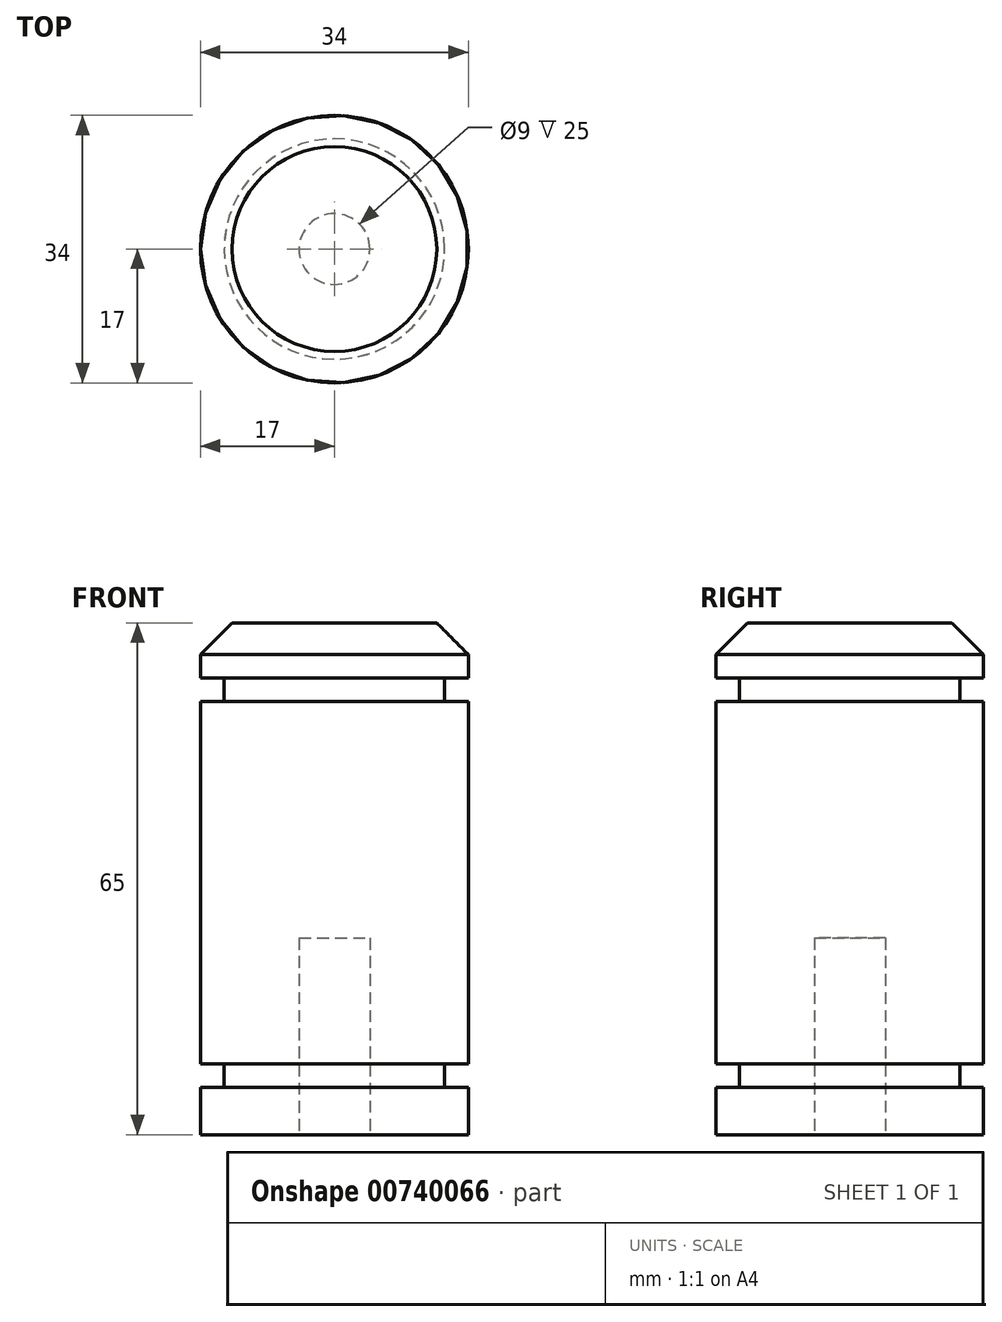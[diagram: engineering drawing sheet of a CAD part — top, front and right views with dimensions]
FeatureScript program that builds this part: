
annotation { "Feature Type Name" : "Feature", "Feature Type Description" : "" }
export const myFeature = defineFeature(function(context is Context, id is Id, definition is map)
    precondition{}
    {
        {
            var Q0;
            Q0=qCreatedBy(makeId("Top.planeOp"),FACE);
            var sketch = newSketch(context, id + "F0", { "sketchPlane" : qUnion([Q0])});
            skCircle(sketch, "E0", {"center": v(0, 0) * mm, "radius": 17 * mm});
            skSolve(sketch);
        }
        {
            var Q0;
            Q0 = qSketchRegion(id + "F0", true);
            extrude(context, id + "F1", {"entities" : qUnion([Q0]), "depth" : 65 * mm, "offsetDistance" : 25 * mm});
        }
        {
            var Q0;
            Q0=makeQuery(id+"F1.opExtrude","CAP_EDGE",EDGE,{"disambiguationData":[OSD([sQuery(id+"F0.wireOp",EDGE,"E0")])],"isStart":false});
            chamfer(context, id + "F2", {"entities" : qUnion([Q0]), "width" : 4 * mm, "tangentPropagation" : true});
        }
        {
            var Q0;
            Q0=makeQuery(id+"F1.opExtrude","CAP_FACE",FACE,{"disambiguationData":[OSD([sQuery(id+"F0.wireOp",EDGE,"E0")])],"isStart":true});
            var sketch = newSketch(context, id + "F3", { "sketchPlane" : qUnion([Q0])});
            skCircle(sketch, "E1", {"center": v(0, 0) * mm, "radius": 4.5 * mm});
            skSolve(sketch);
        }
        {
            var Q0;
            Q0=makeQuery(id+"F3.imprint","IMPRINT",FACE,{"disambiguationData":[TD([[makeQuery(id+"F3.imprint","IMPRINT",EDGE,{"derivedFrom":sQuery(id+"F3.wireOp",EDGE,"E1")}),1.0]])]});
            extrude(context, id + "F4", {"entities" : qUnion([Q0]), "operationType" : NewBodyOperationType.REMOVE, "oppositeDirection" : true, "depth" : 25 * mm, "offsetDistance" : 25 * mm});
        }
        {
            var Q0;
            Q0=qCreatedBy(makeId("Front.planeOp"),FACE);
            var sketch = newSketch(context, id + "F5", { "sketchPlane" : qUnion([Q0])});
            skLineSegment(sketch, "E2.bottom", {"start": v(17, 9) * mm, "end": v(14, 9) * mm});
            skLineSegment(sketch, "E2.top", {"start": v(17, 6) * mm, "end": v(14, 6) * mm});
            skLineSegment(sketch, "E2.left", {"start": v(17, 9) * mm, "end": v(17, 6) * mm});
            skLineSegment(sketch, "E2.right", {"start": v(14, 9) * mm, "end": v(14, 6) * mm});
            skSolve(sketch);
        }
        {
            var Q0;
            Q0 = qSketchRegion(id + "F5", true);
            var Q1;
            Q1=makeQuery(id+"F1.opExtrude","SWEPT_FACE",FACE,{"disambiguationData":[OSD([sQuery(id+"F0.wireOp",EDGE,"E0")])]});
            revolve(context, id + "F6", {"operationType" : NewBodyOperationType.REMOVE, "surfaceOperationType" : NewSurfaceOperationType.NEW, "entities" : qUnion([Q0]), "axis" : qUnion([Q1]), "revolveType" : RevolveType.FULL, "oppositeDirection" : true});
        }
        {
            var Q0;
            Q0=qCreatedBy(makeId("Right.planeOp"),FACE);
            var sketch = newSketch(context, id + "F7", { "sketchPlane" : qUnion([Q0])});
            skLineSegment(sketch, "E3.bottom", {"start": v(-17, 58) * mm, "end": v(-14, 58) * mm});
            skLineSegment(sketch, "E3.top", {"start": v(-17, 55) * mm, "end": v(-14, 55) * mm});
            skLineSegment(sketch, "E3.left", {"start": v(-17, 58) * mm, "end": v(-17, 55) * mm});
            skLineSegment(sketch, "E3.right", {"start": v(-14, 58) * mm, "end": v(-14, 55) * mm});
            skSolve(sketch);
        }
        {
            var Q0;
            Q0 = qSketchRegion(id + "F7", true);
            var Q1;
            {var subQ0=sQuery(id+"F0.wireOp",EDGE,"E0");Q1=makeQuery(id+"F2.opChamfer","BLEND_EDGE",EDGE,{"blendedFrom":[makeQuery(id+"F1.opExtrude","CAP_EDGE",EDGE,{"disambiguationData":[OSD([subQ0])],"isStart":false}),makeQuery(id+"F1.opExtrude","CAP_FACE",FACE,{"disambiguationData":[OSD([subQ0])],"isStart":false})],"blendedInto":[makeQuery(id+"F1.opExtrude","CAP_FACE",FACE,{"disambiguationData":[OSD([subQ0])],"isStart":false})]});}
            revolve(context, id + "F8", {"operationType" : NewBodyOperationType.REMOVE, "surfaceOperationType" : NewSurfaceOperationType.NEW, "entities" : qUnion([Q0]), "axis" : qUnion([Q1]), "revolveType" : RevolveType.FULL, "oppositeDirection" : true});
        }
    });
